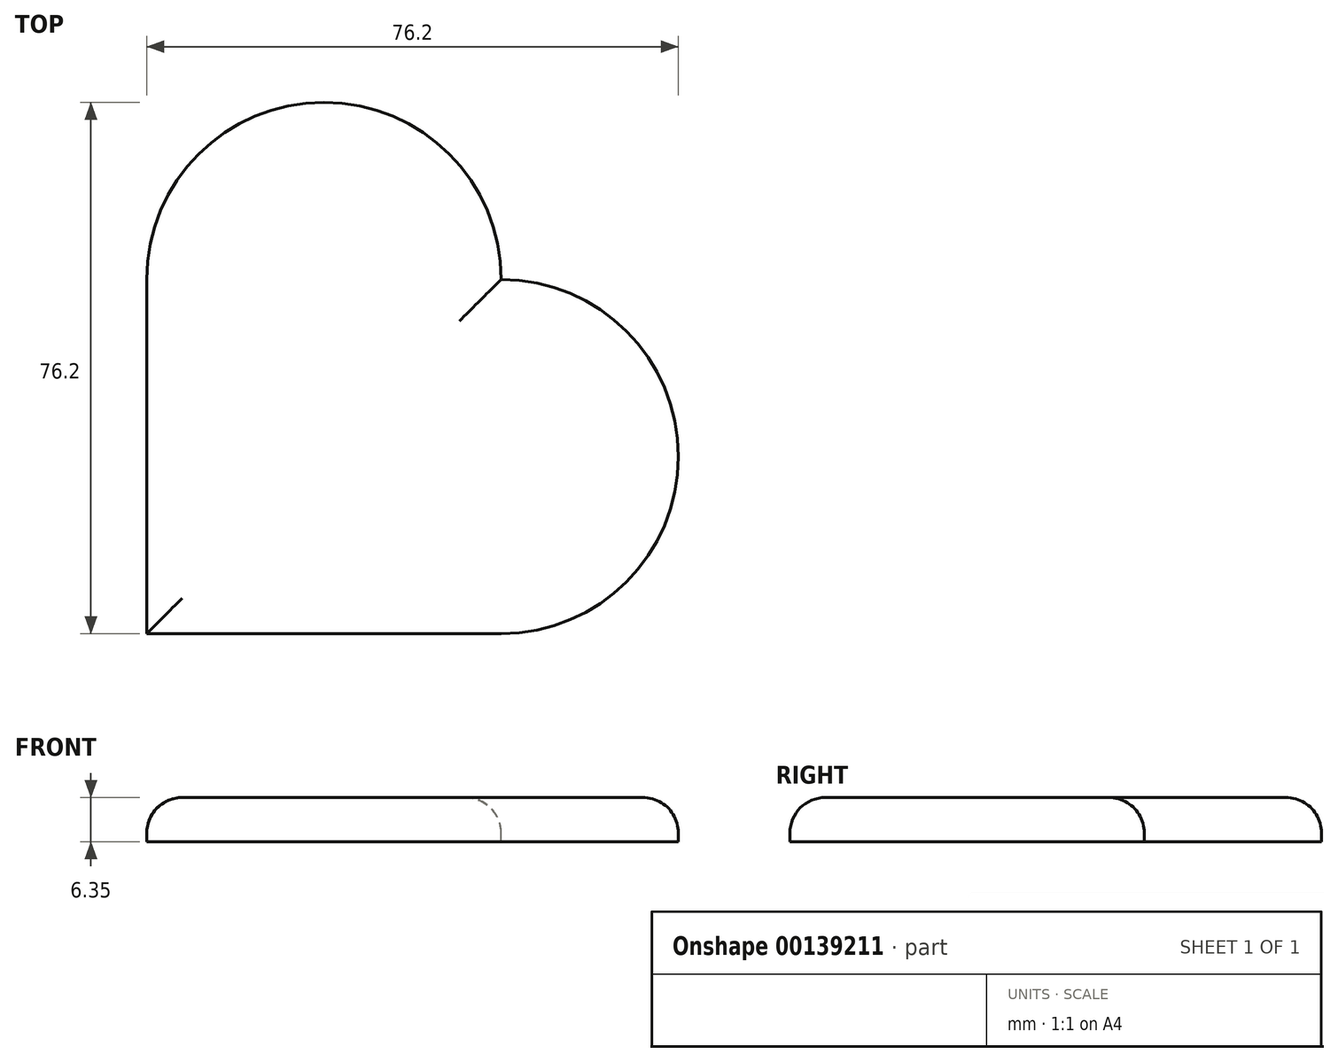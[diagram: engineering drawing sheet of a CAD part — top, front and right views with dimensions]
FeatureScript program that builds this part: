
annotation { "Feature Type Name" : "Feature", "Feature Type Description" : "" }
export const myFeature = defineFeature(function(context is Context, id is Id, definition is map)
    precondition{}
    {
        {
            var Q0;
            Q0=qCreatedBy(makeId("Top.planeOp"),FACE);
            var sketch = newSketch(context, id + "F0", { "sketchPlane" : qUnion([Q0])});
            skLineSegment(sketch, "E0.bottom", {"start": v(25.4, -25.4) * mm, "end": v(-25.4, -25.4) * mm});
            skLineSegment(sketch, "E0.top", {"start": v(25.4, 25.4) * mm, "end": v(-25.4, 25.4) * mm});
            skLineSegment(sketch, "E0.left", {"start": v(25.4, -25.4) * mm, "end": v(25.4, 25.4) * mm});
            skLineSegment(sketch, "E0.right", {"start": v(-25.4, -25.4) * mm, "end": v(-25.4, 25.4) * mm});
            skPoint(sketch, "E0.middle", {"position": v(0, 0) * mm});
            skCircle(sketch, "E1", {"center": v(25.4, 0) * mm, "radius": 25.4 * mm});
            skCircle(sketch, "E2", {"center": v(0, 25.4) * mm, "radius": 25.4 * mm});
            skSolve(sketch);
        }
        {
            var Q0;
            {var subQ0=sQuery(id+"F0.wireOp",EDGE,"E0.bottom");Q0=makeQuery(id+"F0.imprint","IMPRINT",FACE,{"disambiguationData":[TD([[makeQuery(id+"F0.imprint","IMPRINT",EDGE,{"derivedFrom":subQ0}),-1.0]])]});}
            var Q1;
            {var subQ0=sQuery(id+"F0.wireOp",EDGE,"E0.top");Q1=makeQuery(id+"F0.imprint","IMPRINT",FACE,{"disambiguationData":[TD([[makeQuery(id+"F0.imprint","IMPRINT",EDGE,{"derivedFrom":subQ0}),1.0]])]});}
            var Q2;
            {var subQ0=sQuery(id+"F0.wireOp",EDGE,"E2");var subQ1=sQuery(id+"F0.wireOp",EDGE,"E1");var subQ3=makeQuery(id+"F0.imprint","INTERSECT",VERTEX,{"derivedFrom":[subQ1,subQ0]});Q2=makeQuery(id+"F0.imprint","IMPRINT",FACE,{"disambiguationData":[TD([[makeQuery(id+"F0.imprint","IMPRINT",EDGE,{"disambiguationData":[TD([[subQ3,1.0]])],"derivedFrom":subQ1}),1.0]])]});}
            var Q3;
            {var subQ0=sQuery(id+"F0.wireOp",EDGE,"E0.left");Q3=makeQuery(id+"F0.imprint","IMPRINT",FACE,{"disambiguationData":[TD([[makeQuery(id+"F0.imprint","IMPRINT",EDGE,{"derivedFrom":subQ0}),1.0]])]});}
            var Q4;
            {var subQ0=sQuery(id+"F0.wireOp",EDGE,"E0.left");Q4=makeQuery(id+"F0.imprint","IMPRINT",FACE,{"disambiguationData":[TD([[makeQuery(id+"F0.imprint","IMPRINT",EDGE,{"derivedFrom":subQ0}),-1.0]])]});}
            var Q5;
            {var subQ0=sQuery(id+"F0.wireOp",EDGE,"E0.top");Q5=makeQuery(id+"F0.imprint","IMPRINT",FACE,{"disambiguationData":[TD([[makeQuery(id+"F0.imprint","IMPRINT",EDGE,{"derivedFrom":subQ0}),-1.0]])]});}
            extrude(context, id + "F1", {"entities" : qUnion([Q0, Q1, Q2, Q3, Q4, Q5]), "oppositeDirection" : true, "depth" : 6.35 * mm});
        }
        {
            var Q0;
            Q0=makeQuery(id+"F1.opExtrude","CAP_FACE",FACE,{"disambiguationData":[OSD([sQuery(id+"F0.wireOp",EDGE,"E0.bottom"),sQuery(id+"F0.wireOp",EDGE,"E0.right"),sQuery(id+"F0.wireOp",EDGE,"E1"),sQuery(id+"F0.wireOp",EDGE,"E2")])],"isStart":true});
            fillet(context, id + "F2", {"entities" : qUnion([Q0]), "radius" : 5.08 * mm, "tangentPropagation" : true, "rho" : 0, "crossSection" : FilletCrossSection.CONIC, "allowEdgeOverflow" : false});
        }
    });
